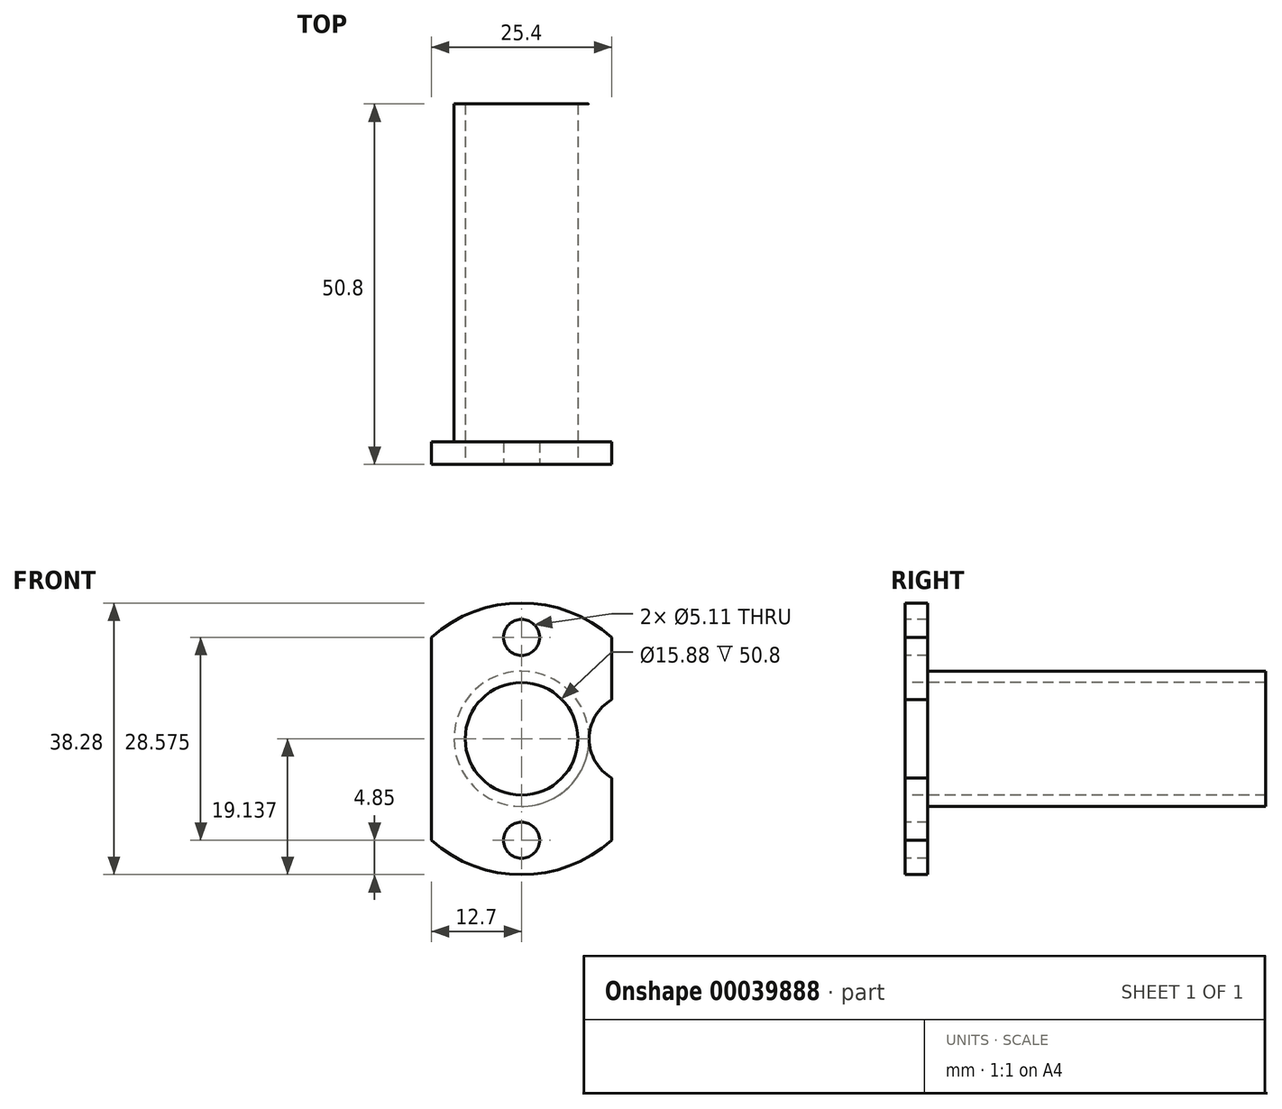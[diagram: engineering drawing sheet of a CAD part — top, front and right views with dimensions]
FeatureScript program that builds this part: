
annotation { "Feature Type Name" : "Feature", "Feature Type Description" : "" }
export const myFeature = defineFeature(function(context is Context, id is Id, definition is map)
    precondition{}
    {
        {
            var Q0;
            Q0=qCreatedBy(makeId("Front.planeOp"),FACE);
            var sketch = newSketch(context, id + "F0", { "sketchPlane" : qUnion([Q0])});
            skLineSegment(sketch, "E0.bottom", {"start": v(0, 0) * mm, "end": v(25.4, 0) * mm, "construction": true});
            skLineSegment(sketch, "E0.top", {"start": v(0, 28.58) * mm, "end": v(25.4, 28.58) * mm, "construction": true});
            skLineSegment(sketch, "E0.left", {"start": v(0, 0) * mm, "end": v(0, 28.58) * mm});
            skLineSegment(sketch, "E0.right", {"start": v(25.4, 0) * mm, "end": v(25.4, 28.58) * mm});
            skPoint(sketch, "E1.visualSharp", {"position": v(25.4, 28.58) * mm});
            skLineSegment(sketch, "E1.filletArc", {"start": v(25.4, 28.58) * mm, "end": v(25.4, 28.58) * mm});
            skArc(sketch, "E2", {"start": v(25.4, 28.58) * mm, "mid": v(12.7, 33.43) * mm, "end": v(0, 28.58) * mm});
            skArc(sketch, "E3", {"start": v(0, 0) * mm, "mid": v(12.7, -4.85) * mm, "end": v(25.4, 0) * mm});
            skLineSegment(sketch, "E4", {"start": v(12.7, 28.58) * mm, "end": v(12.7, 0) * mm, "construction": true});
            skSolve(sketch);
        }
        {
            var Q0;
            Q0=makeQuery(id+"F0.imprint","IMPRINT",FACE,{"disambiguationData":[TD([[makeQuery(id+"F0.imprint","IMPRINT",EDGE,{"derivedFrom":sQuery(id+"F0.wireOp",EDGE,"E0.left")}),-1.0]])]});
            extrude(context, id + "F1", {"entities" : qUnion([Q0]), "oppositeDirection" : true, "depth" : 3.17 * mm});
        }
        {
            var Q0;
            Q0=makeQuery(id+"F1.opExtrude","CAP_FACE",FACE,{"disambiguationData":[OSD([sQuery(id+"F0.wireOp",EDGE,"E0.left"),sQuery(id+"F0.wireOp",EDGE,"E0.right"),sQuery(id+"F0.wireOp",EDGE,"E2"),sQuery(id+"F0.wireOp",EDGE,"E3")])],"isStart":true});
            var sketch = newSketch(context, id + "F2", { "sketchPlane" : qUnion([Q0])});
            skLineSegment(sketch, "E5", {"start": v(25.4, 0) * mm, "end": v(0, 0) * mm, "construction": true});
            skPoint(sketch, "E6.endSnap0", {"position": v(12.7, 33.43) * mm});
            skLineSegment(sketch, "E7", {"start": v(0, 28.58) * mm, "end": v(25.4, 28.58) * mm, "construction": true});
            skLineSegment(sketch, "E8", {"start": v(12.7, 28.58) * mm, "end": v(12.7, 0) * mm, "construction": true});
            skCircle(sketch, "E9", {"center": v(12.7, 28.58) * mm, "radius": 2.55 * mm});
            skCircle(sketch, "E10.0.1.0", {"center": v(12.7, 0) * mm, "radius": 2.55 * mm});
            skLineSegment(sketch, "E10.direction1", {"start": v(12.7, 28.58) * mm, "end": v(38.1, 28.58) * mm, "construction": true});
            skCircle(sketch, "E11", {"center": v(12.7, 14.29) * mm, "radius": 7.94 * mm});
            skLineSegment(sketch, "E12", {"start": v(28.57, 33.9) * mm, "end": v(28.57, -13.55) * mm, "construction": true});
            skLineSegment(sketch, "E13", {"start": v(12.7, 14.29) * mm, "end": v(70.97, 14.29) * mm, "construction": true});
            skArc(sketch, "E14", {"start": v(25.4, 8.79) * mm, "mid": v(22.22, 14.29) * mm, "end": v(25.4, 19.79) * mm});
            skLineSegment(sketch, "E15", {"start": v(25.4, 19.79) * mm, "end": v(25.4, 8.79) * mm});
            skSolve(sketch);
        }
        {
            var Q0;
            Q0 = qSketchRegion(id + "F2", true);
            extrude(context, id + "F3", {"entities" : qUnion([Q0]), "operationType" : NewBodyOperationType.REMOVE, "endBound" : BoundingType.THROUGH_ALL, "oppositeDirection" : true, "depth" : 25.4 * mm});
        }
        {
            var Q0;
            Q0=makeQuery(id+"F1.opExtrude","CAP_FACE",FACE,{"disambiguationData":[OSD([sQuery(id+"F0.wireOp",EDGE,"E0.left"),sQuery(id+"F0.wireOp",EDGE,"E0.right"),sQuery(id+"F0.wireOp",EDGE,"E2"),sQuery(id+"F0.wireOp",EDGE,"E3")])],"isStart":true});
            var sketch = newSketch(context, id + "F4", { "sketchPlane" : qUnion([Q0])});
            skCircle(sketch, "E16", {"center": v(12.7, 14.29) * mm, "radius": 9.53 * mm});
            skCircle(sketch, "E17", {"center": v(12.7, 14.29) * mm, "radius": 7.94 * mm});
            skSolve(sketch);
        }
        {
            var Q0;
            Q0 = qSketchRegion(id + "F4", true);
            extrude(context, id + "F5", {"entities" : qUnion([Q0]), "operationType" : NewBodyOperationType.ADD, "oppositeDirection" : true, "depth" : 50.8 * mm});
        }
    });
